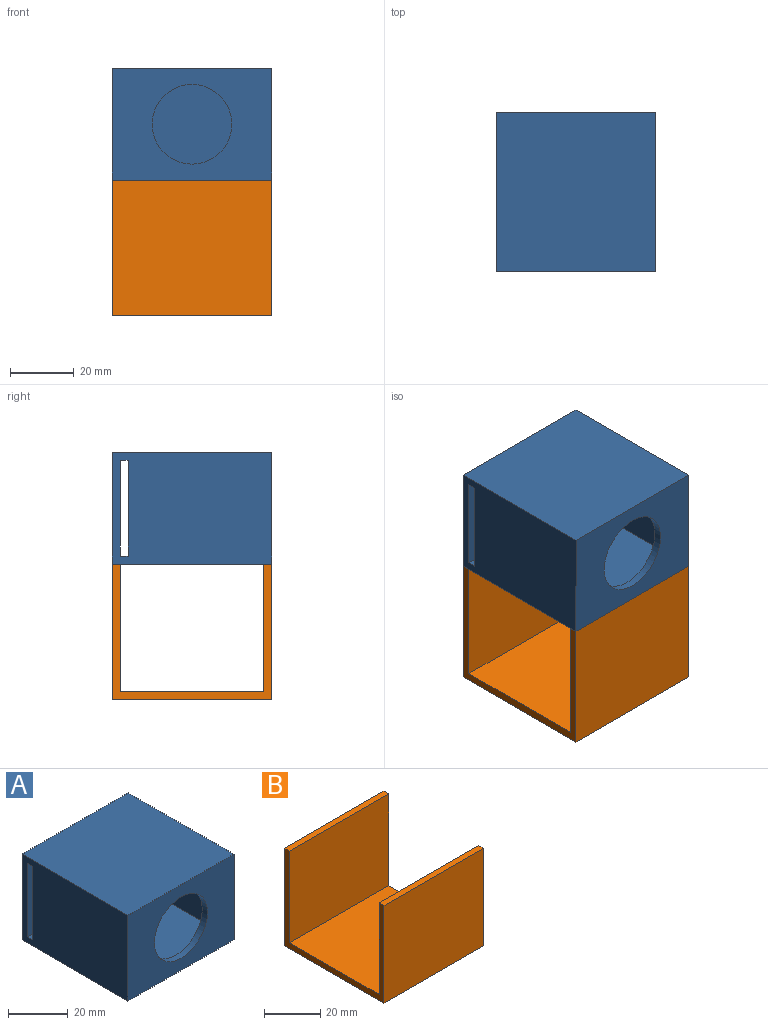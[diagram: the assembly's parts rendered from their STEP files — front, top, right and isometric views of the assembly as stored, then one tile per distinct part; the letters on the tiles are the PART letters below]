
ASSEMBLY  parts=2 mates=1
PART A: 15 faces, bbox 50x50x35 mm
  f0: plane 50x35mm, normal (0,-1,0), area 1259.1mm2, adj f1,f2,f3,f4,f6
  f1: plane 50x50mm, normal (0,0,-1), area 2500mm2, adj f0,f2,f4,f5
  f2: plane 50x35mm, normal (1,0,0), area 1675mm2, adj f0,f1,f3,f5,f8,f10,f12,f13
  f3: plane 50x50mm, normal (0,0,1), area 2500mm2, adj f0,f2,f4,f5
  f4: plane 50x35mm, normal (-1,0,0), area 1675mm2, adj f0,f1,f3,f5,f8,f10,f12,f14
  f5: plane 50x35mm, normal (0,1,0), area 1750mm2, adj f1,f2,f3,f4
  f6: cylinder r=12.5mm len=25mm, axis (0,-1,0), area 196.3mm2, adj f0,f7
  f7: plane 45x30mm, normal (0,1,0), area 859.1mm2, adj f6,f9,f10,f11,f12
  f8: plane 50x30mm, normal (0,-1,0), area 1500mm2, adj f2,f4,f10,f12
  f9: plane 42.5x30mm, normal (1,0,0), area 1275mm2, adj f7,f10,f12,f14
  f10: plane 50x45mm, normal (0,0,-1), area 2037.5mm2, adj f2,f4,f7,f8,f9,f11,f13,f14
  f11: plane 42.5x30mm, normal (-1,0,0), area 1275mm2, adj f7,f10,f12,f13
  f12: plane 50x45mm, normal (0,0,1), area 2037.5mm2, adj f2,f4,f7,f8,f9,f11,f13,f14
  f13: plane 30x2.5mm, normal (0,1,0), area 75mm2, adj f2,f10,f11,f12
  f14: plane 30x2.5mm, normal (0,1,0), area 75mm2, adj f4,f9,f10,f12
PART B: 10 faces, bbox 50x50x42.5 mm
  f0: plane 50x42.5mm, normal (1,0,0), area 325mm2, adj f2,f3,f4,f5,f6,f7,f8,f9
  f1: plane 50x42.5mm, normal (-1,0,0), area 325mm2, adj f2,f3,f4,f5,f6,f7,f8,f9
  f2: plane 50x45mm, normal (0,0,1), area 2250mm2, adj f0,f1,f4,f7
  f3: plane 50x50mm, normal (0,0,-1), area 2500mm2, adj f0,f1,f5,f8
  f4: plane 50x40mm, normal (0,1,0), area 2000mm2, adj f0,f1,f2,f6
  f5: plane 50x42.5mm, normal (0,-1,0), area 2125mm2, adj f0,f1,f3,f6
  f6: plane 50x2.5mm, normal (0,0,1), area 125mm2, adj f0,f1,f4,f5
  f7: plane 50x40mm, normal (0,-1,0), area 2000mm2, adj f0,f1,f2,f9
  f8: plane 50x42.5mm, normal (0,1,0), area 2125mm2, adj f0,f1,f3,f9
  f9: plane 50x2.5mm, normal (0,0,1), area 125mm2, adj f0,f1,f7,f8
PLACE A t=(0,-25,60)mm
PLACE B at identity fixed
MATE fastened A.f1 <-> B.f9  axis (0,0,-1) through (0,25,42.5)mm
